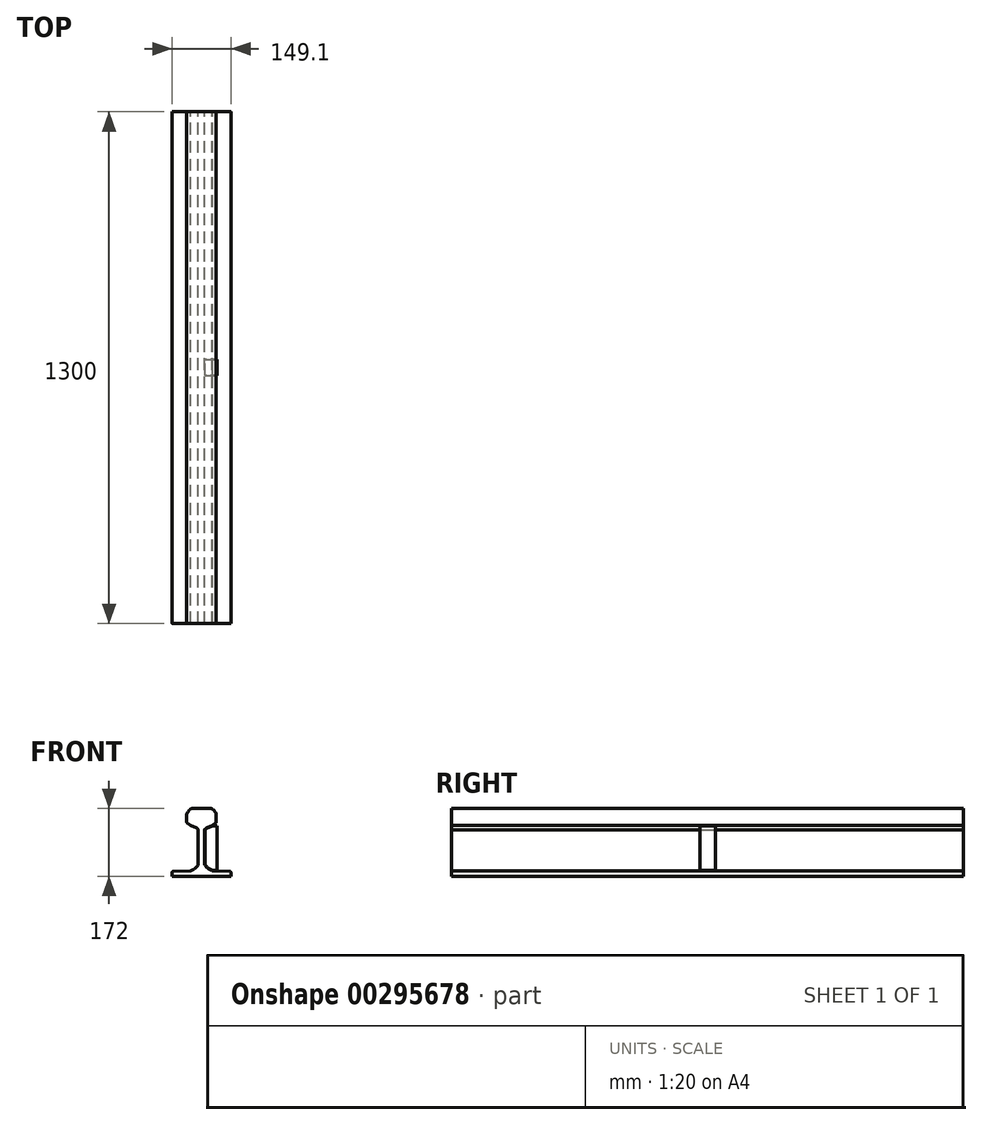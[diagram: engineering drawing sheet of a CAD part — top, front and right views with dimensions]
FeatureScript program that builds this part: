
annotation { "Feature Type Name" : "Feature", "Feature Type Description" : "" }
export const myFeature = defineFeature(function(context is Context, id is Id, definition is map)
    precondition{}
    {
        {
            var Q0;
            Q0=qCreatedBy(makeId("Front.planeOp"),FACE);
            var sketch = newSketch(context, id + "F0", { "sketchPlane" : qUnion([Q0])});
            skLineSegment(sketch, "E0", {"start": v(-10.77, 99.61) * mm, "end": v(-10.77, -103.46) * mm, "construction": true});
            skPoint(sketch, "E1", {"position": v(-86.22, -75.65) * mm});
            skLineSegment(sketch, "E2", {"start": v(-86.22, -75.65) * mm, "end": v(63.78, -75.65) * mm});
            skLineSegment(sketch, "E3", {"start": v(63.78, -75.65) * mm, "end": v(63.78, -66.07) * mm});
            skLineSegment(sketch, "E4", {"start": v(61.86, -64.07) * mm, "end": v(16.54, -62.24) * mm});
            skLineSegment(sketch, "E5", {"start": v(16.54, -62.24) * mm, "end": v(11.83, -59.9) * mm});
            skLineSegment(sketch, "E6", {"start": v(2.23, 47.15) * mm, "end": v(17.09, 53.37) * mm});
            skLineSegment(sketch, "E7", {"start": v(10.83, 96.35) * mm, "end": v(-10.77, 96.35) * mm});
            skLineSegment(sketch, "E8", {"start": v(26.68, 79.78) * mm, "end": v(26.68, 62.41) * mm});
            skLineSegment(sketch, "E9", {"start": v(25.54, 60.06) * mm, "end": v(17.09, 53.37) * mm});
            skLineSegment(sketch, "E10", {"start": v(23.84, 87.88) * mm, "end": v(21, 91.46) * mm});
            skLineSegment(sketch, "E11", {"start": v(-10.77, 3.53) * mm, "end": v(-2.52, 3.53) * mm});
            skLineSegment(sketch, "E12", {"start": v(-2.52, 41.69) * mm, "end": v(-2.52, -46.1) * mm});
            skLineSegment(sketch, "E13", {"start": v(-2.52, 41.69) * mm, "end": v(-1.18, 44.1) * mm});
            skLineSegment(sketch, "E14.MirrorCS", {"start": v(-32.37, 96.35) * mm, "end": v(-10.77, 96.35) * mm});
            skLineSegment(sketch, "E15.MirrorCS", {"start": v(-45.39, 87.88) * mm, "end": v(-42.54, 91.46) * mm});
            skLineSegment(sketch, "E16.MirrorCS", {"start": v(-47.09, 60.06) * mm, "end": v(-38.63, 53.37) * mm});
            skLineSegment(sketch, "E17.MirrorCS", {"start": v(-23.78, 47.15) * mm, "end": v(-38.63, 53.37) * mm});
            skLineSegment(sketch, "E18.MirrorCS", {"start": v(-48.22, 79.78) * mm, "end": v(-48.22, 62.41) * mm});
            skLineSegment(sketch, "E19.MirrorCS", {"start": v(-19.02, 41.69) * mm, "end": v(-20.37, 44.1) * mm});
            skLineSegment(sketch, "E20.MirrorCS", {"start": v(-19.02, 41.69) * mm, "end": v(-19.02, -46.1) * mm});
            skLineSegment(sketch, "E21.MirrorCS", {"start": v(-38.08, -62.24) * mm, "end": v(-33.38, -59.9) * mm});
            skLineSegment(sketch, "E22.MirrorCS", {"start": v(-83.4, -64.07) * mm, "end": v(-38.08, -62.24) * mm});
            skLineSegment(sketch, "E23.MirrorCS", {"start": v(-85.32, -75.65) * mm, "end": v(-85.32, -66.07) * mm});
            skPoint(sketch, "E24.visualSharp", {"position": v(-38.63, 96.35) * mm});
            skArc(sketch, "E24.filletArc", {"start": v(-32.37, 96.35) * mm, "mid": v(-38.01, 95.06) * mm, "end": v(-42.54, 91.46) * mm});
            skPoint(sketch, "E25.visualSharp", {"position": v(17.09, 96.35) * mm});
            skArc(sketch, "E25.filletArc", {"start": v(21, 91.46) * mm, "mid": v(16.47, 95.06) * mm, "end": v(10.83, 96.35) * mm});
            skPoint(sketch, "E26.visualSharp", {"position": v(-48.22, 84.32) * mm});
            skArc(sketch, "E26.filletArc", {"start": v(-45.39, 87.88) * mm, "mid": v(-47.5, 84.07) * mm, "end": v(-48.22, 79.78) * mm});
            skPoint(sketch, "E27.visualSharp", {"position": v(26.68, 84.32) * mm});
            skArc(sketch, "E27.filletArc", {"start": v(26.68, 79.78) * mm, "mid": v(25.95, 84.07) * mm, "end": v(23.84, 87.88) * mm});
            skPoint(sketch, "E28.visualSharp", {"position": v(-48.22, 60.96) * mm});
            skArc(sketch, "E28.filletArc", {"start": v(-48.22, 62.41) * mm, "mid": v(-47.92, 61.1) * mm, "end": v(-47.09, 60.06) * mm});
            skPoint(sketch, "E29.visualSharp", {"position": v(26.68, 60.96) * mm});
            skArc(sketch, "E29.filletArc", {"start": v(25.54, 60.06) * mm, "mid": v(26.38, 61.1) * mm, "end": v(26.68, 62.41) * mm});
            skPoint(sketch, "E30.visualSharp", {"position": v(0, 46.21) * mm});
            skArc(sketch, "E30.filletArc", {"start": v(2.23, 47.15) * mm, "mid": v(0.27, 45.9) * mm, "end": v(-1.18, 44.1) * mm});
            skPoint(sketch, "E31.visualSharp", {"position": v(-21.55, 46.21) * mm});
            skArc(sketch, "E31.filletArc", {"start": v(-20.37, 44.1) * mm, "mid": v(-21.82, 45.9) * mm, "end": v(-23.78, 47.15) * mm});
            skPoint(sketch, "E32.visualSharp", {"position": v(-85.32, -64.15) * mm});
            skArc(sketch, "E32.filletArc", {"start": v(-83.4, -64.07) * mm, "mid": v(-84.77, -64.69) * mm, "end": v(-85.32, -66.07) * mm});
            skPoint(sketch, "E33.visualSharp", {"position": v(63.78, -64.15) * mm});
            skArc(sketch, "E33.filletArc", {"start": v(63.78, -66.07) * mm, "mid": v(63.22, -64.69) * mm, "end": v(61.86, -64.07) * mm});
            skArc(sketch, "E34.filletArc", {"start": v(-33.38, -59.9) * mm, "mid": v(-25.48, -54.5) * mm, "end": v(-19.33, -47.17) * mm});
            skArc(sketch, "E35.filletArc", {"start": v(-19.33, -47.17) * mm, "mid": v(-19.1, -46.66) * mm, "end": v(-19.02, -46.1) * mm});
            skPoint(sketch, "E36.visualSharp", {"position": v(0, -54) * mm});
            skArc(sketch, "E36.filletArc", {"start": v(-2.22, -47.17) * mm, "mid": v(3.93, -54.5) * mm, "end": v(11.83, -59.9) * mm});
            skPoint(sketch, "E37.visualSharp", {"position": v(-2.52, -46.67) * mm});
            skArc(sketch, "E37.filletArc", {"start": v(-2.52, -46.1) * mm, "mid": v(-2.45, -46.66) * mm, "end": v(-2.22, -47.17) * mm});
            skLineSegment(sketch, "E38.0", {"start": v(2.66, 46.13) * mm, "end": v(17.51, 52.36) * mm});
            skArc(sketch, "E38.1", {"start": v(2.66, 46.13) * mm, "mid": v(1, 45.09) * mm, "end": v(-0.22, 43.56) * mm});
            skLineSegment(sketch, "E38.2", {"start": v(-1.42, 41.4) * mm, "end": v(-0.22, 43.56) * mm});
            skLineSegment(sketch, "E38.3", {"start": v(-1.42, 41.4) * mm, "end": v(-1.42, -46.1) * mm});
            skLineSegment(sketch, "E38.5", {"start": v(16.82, -61.15) * mm, "end": v(12.32, -58.9) * mm});
            skArc(sketch, "E38.6", {"start": v(-1.29, -46.58) * mm, "mid": v(4.67, -53.69) * mm, "end": v(12.32, -58.9) * mm});
            skArc(sketch, "E38.7", {"start": v(-1.42, -46.1) * mm, "mid": v(-1.39, -46.35) * mm, "end": v(-1.29, -46.58) * mm});
            skLineSegment(sketch, "E39.0", {"start": v(28.24, -61.61) * mm, "end": v(16.82, -61.15) * mm});
            skLineSegment(sketch, "E40", {"start": v(17.51, 52.36) * mm, "end": v(28.24, 52.36) * mm});
            skLineSegment(sketch, "E41", {"start": v(28.24, 52.36) * mm, "end": v(28.24, -61.61) * mm});
            skSolve(sketch);
        }
        {
            var Q0;
            Q0 = qSketchRegion(id + "F0", true);
            extrude(context, id + "F1", {"entities" : qUnion([Q0]), "depth" : 1300 * mm, "symmetric" : true});
        }
        {
            var Q0;
            Q0=makeQuery(id+"F0.imprint","IMPRINT",FACE,{"disambiguationData":[TD([[makeQuery(id+"F0.imprint","IMPRINT",EDGE,{"derivedFrom":sQuery(id+"F0.wireOp",EDGE,"E38.0")}),-1.0]])]});
            extrude(context, id + "F2", {"entities" : qUnion([Q0]), "operationType" : NewBodyOperationType.REMOVE, "oppositeDirection" : true, "depth" : 1300 * mm, "symmetric" : true});
        }
        {
            var Q0;
            Q0=makeQuery(id+"F0.imprint","IMPRINT",FACE,{"disambiguationData":[TD([[makeQuery(id+"F0.imprint","IMPRINT",EDGE,{"derivedFrom":sQuery(id+"F0.wireOp",EDGE,"E38.0")}),-1.0]])]});
            extrude(context, id + "F3", {"entities" : qUnion([Q0]), "depth" : 40 * mm, "symmetric" : true});
        }
    });
